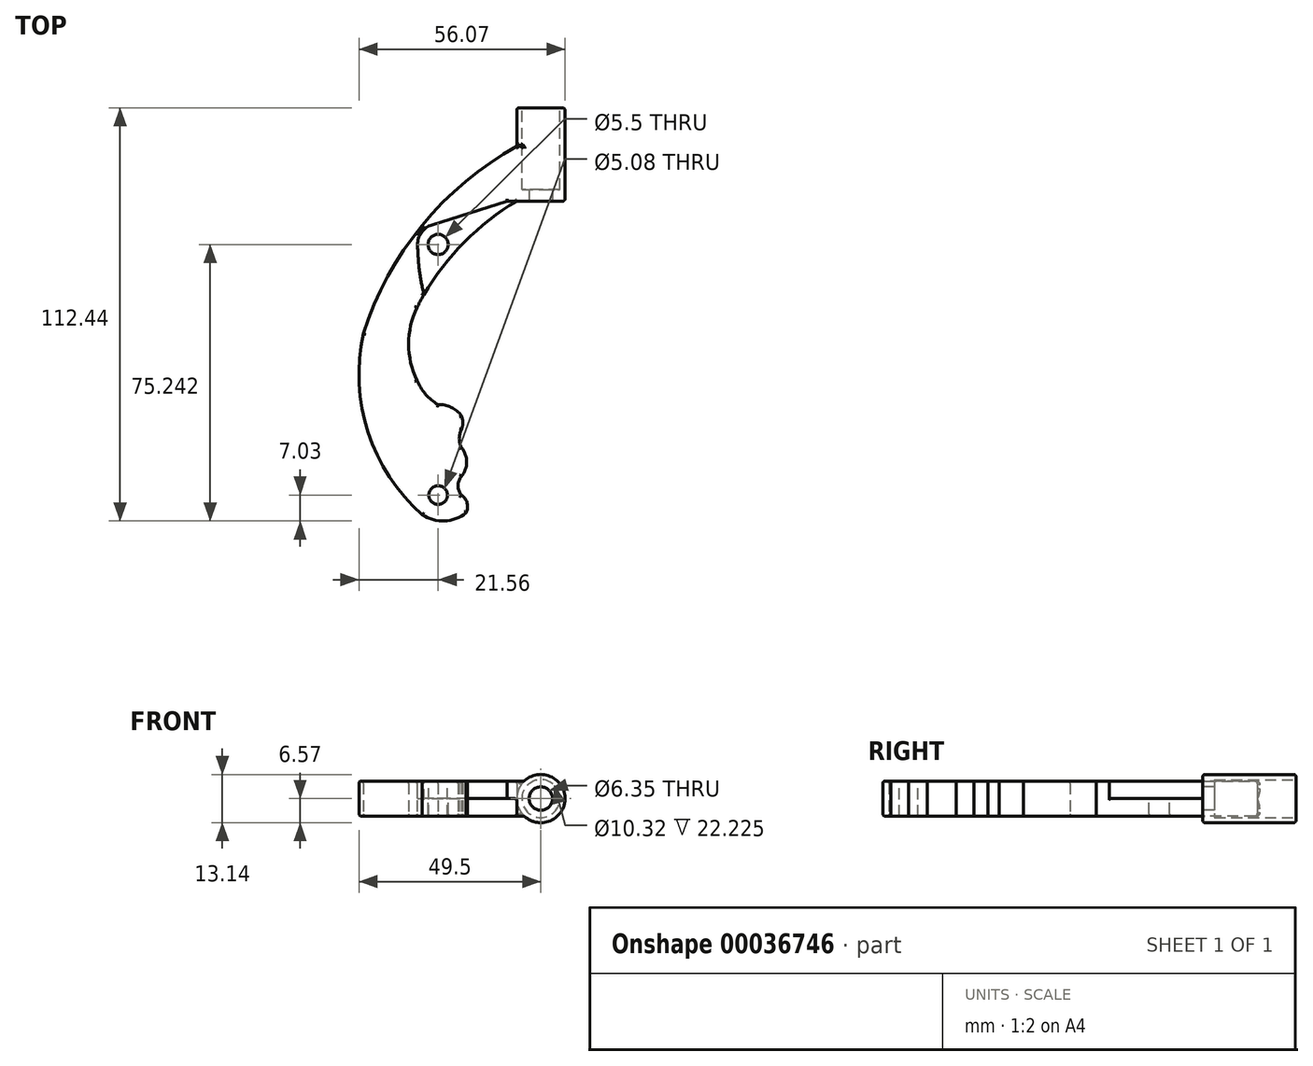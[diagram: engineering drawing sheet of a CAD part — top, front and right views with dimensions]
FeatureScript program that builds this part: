
annotation { "Feature Type Name" : "Feature", "Feature Type Description" : "" }
export const myFeature = defineFeature(function(context is Context, id is Id, definition is map)
    precondition{}
    {
        {
            var Q0;
            Q0=qCreatedBy(makeId("Top.planeOp"),FACE);
            var sketch = newSketch(context, id + "F0", { "sketchPlane" : qUnion([Q0])});
            skArc(sketch, "E0", {"start": v(-6.57, 0) * mm, "mid": v(-22.16, -12.58) * mm, "end": v(-33.7, -28.96) * mm});
            skArc(sketch, "E1", {"start": v(-33.7, -28.96) * mm, "mid": v(-35.96, -38.86) * mm, "end": v(-33.7, -48.77) * mm});
            skArc(sketch, "E2", {"start": v(-33.7, -48.77) * mm, "mid": v(-31.35, -52.53) * mm, "end": v(-27.94, -55.37) * mm});
            skArc(sketch, "E3", {"start": v(-21.59, -58.42) * mm, "mid": v(-24.4, -56.12) * mm, "end": v(-27.94, -55.37) * mm});
            skArc(sketch, "E4", {"start": v(-21.59, -62.23) * mm, "mid": v(-21.22, -60.33) * mm, "end": v(-21.59, -58.42) * mm});
            skArc(sketch, "E5", {"start": v(-21.59, -62.23) * mm, "mid": v(-22.2, -64.64) * mm, "end": v(-21.59, -67.06) * mm});
            skArc(sketch, "E6", {"start": v(-21.6, -74.93) * mm, "mid": v(-20.2, -71) * mm, "end": v(-21.59, -67.06) * mm});
            skArc(sketch, "E7", {"start": v(-21.59, -74.93) * mm, "mid": v(-22.56, -77.47) * mm, "end": v(-21.59, -80.01) * mm});
            skArc(sketch, "E8", {"start": v(-20.32, -84.84) * mm, "mid": v(-20.05, -82.19) * mm, "end": v(-21.6, -80.01) * mm});
            skArc(sketch, "E9", {"start": v(-32.26, -85.34) * mm, "mid": v(-26.2, -87.03) * mm, "end": v(-20.32, -84.84) * mm});
            skArc(sketch, "E10", {"start": v(-48.26, -36.07) * mm, "mid": v(-47.01, -62.9) * mm, "end": v(-32.26, -85.34) * mm});
            skArc(sketch, "E11", {"start": v(-6.57, 14.92) * mm, "mid": v(-32.31, -6.57) * mm, "end": v(-48.26, -36.07) * mm});
            skLineSegment(sketch, "E12", {"start": v(-6.57, 0) * mm, "end": v(0, 0) * mm});
            skLineSegment(sketch, "E13", {"start": v(0, 0) * mm, "end": v(0, 14.92) * mm});
            skLineSegment(sketch, "E14", {"start": v(0, 14.92) * mm, "end": v(-6.57, 14.92) * mm});
            skSolve(sketch);
        }
        {
            var Q0;
            Q0 = qSketchRegion(id + "F0", true);
            extrude(context, id + "F1", {"entities" : qUnion([Q0]), "endBound" : BoundingType.SYMMETRIC, "depth" : 9.52 * mm});
        }
        {
            var Q0;
            Q0=qCreatedBy(makeId("Front.planeOp"),FACE);
            var sketch = newSketch(context, id + "F2", { "sketchPlane" : qUnion([Q0])});
            skCircle(sketch, "E15", {"center": v(0, 0) * mm, "radius": 6.57 * mm});
            skSolve(sketch);
        }
        {
            var Q0;
            Q0 = qSketchRegion(id + "F2", true);
            extrude(context, id + "F3", {"entities" : qUnion([Q0]), "operationType" : NewBodyOperationType.ADD, "oppositeDirection" : true, "depth" : 25.4 * mm});
        }
        {
            var Q0;
            Q0=qCreatedBy(makeId("Front.planeOp"),FACE);
            var sketch = newSketch(context, id + "F4", { "sketchPlane" : qUnion([Q0])});
            skCircle(sketch, "E16", {"center": v(0, 0) * mm, "radius": 3.18 * mm});
            skSolve(sketch);
        }
        {
            var Q0;
            Q0 = qSketchRegion(id + "F4", true);
            extrude(context, id + "F5", {"entities" : qUnion([Q0]), "operationType" : NewBodyOperationType.REMOVE, "endBound" : BoundingType.THROUGH_ALL, "oppositeDirection" : true, "depth" : 25.4 * mm});
        }
        {
            var Q0;
            Q0=makeQuery(id+"F3.opExtrude","CAP_FACE",FACE,{"disambiguationData":[OSD([sQuery(id+"F2.wireOp",EDGE,"E15")])],"isStart":false});
            var sketch = newSketch(context, id + "F6", { "sketchPlane" : qUnion([Q0])});
            skCircle(sketch, "E17", {"center": v(0, 0) * mm, "radius": 5.16 * mm});
            skSolve(sketch);
        }
        {
            var Q0;
            Q0 = qSketchRegion(id + "F6", true);
            extrude(context, id + "F7", {"entities" : qUnion([Q0]), "operationType" : NewBodyOperationType.REMOVE, "oppositeDirection" : true, "depth" : 22.22 * mm});
        }
        {
            var Q0;
            Q0=makeQuery(id+"F1.opExtrude","CAP_FACE",FACE,{"disambiguationData":[OSD([sQuery(id+"F0.wireOp",EDGE,"E0"),sQuery(id+"F0.wireOp",EDGE,"E1"),sQuery(id+"F0.wireOp",EDGE,"E2"),sQuery(id+"F0.wireOp",EDGE,"E3"),sQuery(id+"F0.wireOp",EDGE,"E4"),sQuery(id+"F0.wireOp",EDGE,"E5"),sQuery(id+"F0.wireOp",EDGE,"E6"),sQuery(id+"F0.wireOp",EDGE,"E7"),sQuery(id+"F0.wireOp",EDGE,"E8"),sQuery(id+"F0.wireOp",EDGE,"E9"),sQuery(id+"F0.wireOp",EDGE,"E10"),sQuery(id+"F0.wireOp",EDGE,"E11"),sQuery(id+"F0.wireOp",EDGE,"E12"),sQuery(id+"F0.wireOp",EDGE,"E13"),sQuery(id+"F0.wireOp",EDGE,"E14")])],"isStart":false});
            var sketch = newSketch(context, id + "F8", { "sketchPlane" : qUnion([Q0])});
            skCircle(sketch, "E18", {"center": v(-27.94, -11.8) * mm, "radius": 2.75 * mm});
            skSolve(sketch);
        }
        {
            var Q0;
            Q0 = qSketchRegion(id + "F8", true);
            extrude(context, id + "F9", {"entities" : qUnion([Q0]), "operationType" : NewBodyOperationType.REMOVE, "endBound" : BoundingType.THROUGH_ALL, "oppositeDirection" : true, "depth" : 25.4 * mm});
        }
        {
            var Q0;
            Q0=makeQuery(id+"F1.opExtrude","CAP_FACE",FACE,{"disambiguationData":[OSD([sQuery(id+"F0.wireOp",EDGE,"E0"),sQuery(id+"F0.wireOp",EDGE,"E1"),sQuery(id+"F0.wireOp",EDGE,"E2"),sQuery(id+"F0.wireOp",EDGE,"E3"),sQuery(id+"F0.wireOp",EDGE,"E4"),sQuery(id+"F0.wireOp",EDGE,"E5"),sQuery(id+"F0.wireOp",EDGE,"E6"),sQuery(id+"F0.wireOp",EDGE,"E7"),sQuery(id+"F0.wireOp",EDGE,"E8"),sQuery(id+"F0.wireOp",EDGE,"E9"),sQuery(id+"F0.wireOp",EDGE,"E10"),sQuery(id+"F0.wireOp",EDGE,"E11"),sQuery(id+"F0.wireOp",EDGE,"E12"),sQuery(id+"F0.wireOp",EDGE,"E13"),sQuery(id+"F0.wireOp",EDGE,"E14")])],"isStart":false});
            var sketch = newSketch(context, id + "F10", { "sketchPlane" : qUnion([Q0])});
            skArc(sketch, "E19", {"start": v(-29.62, -6.47) * mm, "mid": v(-32.48, -8.54) * mm, "end": v(-33.53, -11.9) * mm});
            skLineSegment(sketch, "E20", {"start": v(-29.62, -6.47) * mm, "end": v(-9.11, 0) * mm});
            skLineSegment(sketch, "E21", {"start": v(-9.11, 0) * mm, "end": v(-6.57, 0) * mm});
            skLineSegment(sketch, "E22", {"start": v(-6.57, 0) * mm, "end": v(-30.99, -27.94) * mm});
            skArc(sketch, "E23", {"start": v(-33.53, -11.9) * mm, "mid": v(-33.37, -15.48) * mm, "end": v(-33.02, -19.05) * mm});
            skArc(sketch, "E24", {"start": v(-33.02, -19.05) * mm, "mid": v(-32.23, -23.55) * mm, "end": v(-30.99, -27.94) * mm});
            skSolve(sketch);
        }
        {
            var Q0;
            Q0 = qSketchRegion(id + "F10", true);
            extrude(context, id + "F11", {"entities" : qUnion([Q0]), "operationType" : NewBodyOperationType.REMOVE, "oppositeDirection" : true, "depth" : 4.76 * mm});
        }
        {
            var Q0;
            Q0=makeQuery(id+"F1.opExtrude","CAP_EDGE",EDGE,{"disambiguationData":[OSD([sQuery(id+"F0.wireOp",EDGE,"E11")])],"isStart":false});
            var Q1;
            Q1=makeQuery(id+"F1.opExtrude","CAP_EDGE",EDGE,{"disambiguationData":[OSD([sQuery(id+"F0.wireOp",EDGE,"E10")])],"isStart":false});
            var Q2;
            Q2=makeQuery(id+"F1.opExtrude","CAP_EDGE",EDGE,{"disambiguationData":[OSD([sQuery(id+"F0.wireOp",EDGE,"E10")])],"isStart":true});
            var Q3;
            Q3=makeQuery(id+"F1.opExtrude","CAP_EDGE",EDGE,{"disambiguationData":[OSD([sQuery(id+"F0.wireOp",EDGE,"E11")])],"isStart":true});
            var Q4;
            Q4=makeQuery(id+"F1.opExtrude","CAP_EDGE",EDGE,{"disambiguationData":[OSD([sQuery(id+"F0.wireOp",EDGE,"E9")])],"isStart":false});
            var Q5;
            Q5=makeQuery(id+"F1.opExtrude","CAP_EDGE",EDGE,{"disambiguationData":[OSD([sQuery(id+"F0.wireOp",EDGE,"E9")])],"isStart":true});
            var Q6;
            Q6=makeQuery(id+"F1.opExtrude","CAP_FACE",FACE,{"disambiguationData":[OSD([sQuery(id+"F0.wireOp",EDGE,"E0"),sQuery(id+"F0.wireOp",EDGE,"E1"),sQuery(id+"F0.wireOp",EDGE,"E2"),sQuery(id+"F0.wireOp",EDGE,"E3"),sQuery(id+"F0.wireOp",EDGE,"E4"),sQuery(id+"F0.wireOp",EDGE,"E5"),sQuery(id+"F0.wireOp",EDGE,"E6"),sQuery(id+"F0.wireOp",EDGE,"E7"),sQuery(id+"F0.wireOp",EDGE,"E8"),sQuery(id+"F0.wireOp",EDGE,"E9"),sQuery(id+"F0.wireOp",EDGE,"E10"),sQuery(id+"F0.wireOp",EDGE,"E11"),sQuery(id+"F0.wireOp",EDGE,"E12"),sQuery(id+"F0.wireOp",EDGE,"E13"),sQuery(id+"F0.wireOp",EDGE,"E14")])],"isStart":true});
            var Q7;
            Q7=makeQuery(id+"F1.opExtrude","CAP_FACE",FACE,{"disambiguationData":[OSD([sQuery(id+"F0.wireOp",EDGE,"E0"),sQuery(id+"F0.wireOp",EDGE,"E1"),sQuery(id+"F0.wireOp",EDGE,"E2"),sQuery(id+"F0.wireOp",EDGE,"E3"),sQuery(id+"F0.wireOp",EDGE,"E4"),sQuery(id+"F0.wireOp",EDGE,"E5"),sQuery(id+"F0.wireOp",EDGE,"E6"),sQuery(id+"F0.wireOp",EDGE,"E7"),sQuery(id+"F0.wireOp",EDGE,"E8"),sQuery(id+"F0.wireOp",EDGE,"E9"),sQuery(id+"F0.wireOp",EDGE,"E10"),sQuery(id+"F0.wireOp",EDGE,"E11"),sQuery(id+"F0.wireOp",EDGE,"E12"),sQuery(id+"F0.wireOp",EDGE,"E13"),sQuery(id+"F0.wireOp",EDGE,"E14")])],"isStart":false});
            var Q8;
            Q8=makeQuery(id+"F3.opExtrude","SWEPT_FACE",FACE,{"disambiguationData":[OSD([sQuery(id+"F2.wireOp",EDGE,"E15")])]});
            fillet(context, id + "F12", {"entities" : qUnion([Q0, Q1, Q2, Q3, Q4, Q5, Q6, Q7, Q8]), "radius" : 0.64 * mm, "tangentPropagation" : true, "allowEdgeOverflow" : false});
        }
        {
            var Q0;
            Q0=makeQuery(id+"F11.boolean.opBoolean","INTERSECT",EDGE,{"derivedFrom":[makeQuery(id+"F1.opExtrude","SWEPT_FACE",FACE,{"disambiguationData":[OSD([sQuery(id+"F0.wireOp",EDGE,"E0")])]}),makeQuery(id+"F11.opExtrude","CAP_FACE",FACE,{"disambiguationData":[OSD([sQuery(id+"F10.wireOp",EDGE,"E19"),sQuery(id+"F10.wireOp",EDGE,"E20"),sQuery(id+"F10.wireOp",EDGE,"E21"),sQuery(id+"F10.wireOp",EDGE,"E22"),sQuery(id+"F10.wireOp",EDGE,"E23"),sQuery(id+"F10.wireOp",EDGE,"E24")])],"isStart":false})]});
            fillet(context, id + "F13", {"entities" : qUnion([Q0]), "radius" : 0.38 * mm, "tangentPropagation" : true, "allowEdgeOverflow" : false});
        }
        {
            var Q0;
            Q0=makeQuery(id+"F12.opFillet","SPLIT",FACE,{"disambiguationData":[OD(0.0)],"derivedFrom":makeQuery(id+"F1.opExtrude","CAP_FACE",FACE,{"disambiguationData":[OSD([sQuery(id+"F0.wireOp",EDGE,"E0"),sQuery(id+"F0.wireOp",EDGE,"E1"),sQuery(id+"F0.wireOp",EDGE,"E2"),sQuery(id+"F0.wireOp",EDGE,"E3"),sQuery(id+"F0.wireOp",EDGE,"E4"),sQuery(id+"F0.wireOp",EDGE,"E5"),sQuery(id+"F0.wireOp",EDGE,"E6"),sQuery(id+"F0.wireOp",EDGE,"E7"),sQuery(id+"F0.wireOp",EDGE,"E8"),sQuery(id+"F0.wireOp",EDGE,"E9"),sQuery(id+"F0.wireOp",EDGE,"E10"),sQuery(id+"F0.wireOp",EDGE,"E11"),sQuery(id+"F0.wireOp",EDGE,"E12"),sQuery(id+"F0.wireOp",EDGE,"E13"),sQuery(id+"F0.wireOp",EDGE,"E14")])],"isStart":false})});
            var sketch = newSketch(context, id + "F14", { "sketchPlane" : qUnion([Q0])});
            skCircle(sketch, "E25", {"center": v(-27.94, -80.01) * mm, "radius": 2.54 * mm});
            skSolve(sketch);
        }
        {
            var Q0;
            Q0 = qSketchRegion(id + "F14", true);
            extrude(context, id + "F15", {"entities" : qUnion([Q0]), "operationType" : NewBodyOperationType.REMOVE, "endBound" : BoundingType.THROUGH_ALL, "oppositeDirection" : true, "depth" : 25.4 * mm});
        }
    });
